# Revit family: Mixer-Basin-Dorf Epic-Wall1
name_source: partatom
category: Plumbing Fixtures
revit_build: Autodesk Revit Architecture 2012 (Build: 20110916_2132(x64)
units: mm (PartAtom-declared; Revit-internal decimal feet)

## types (2) — shared parameters
Assembly Code = D2020300
CW Connection = Yes
CWFU = 2
Connector Radius = 10 mm  [stored 0.0328084 ft]
Default Elevation = 1200 mm
Description = Fully featured cartridge, Chrome finish, Water efficient, Longer reach for sink versatility, European hoses
HW Connection = Yes
HWFU = 2
Manufacturer = Dorf
Material_ANZRS = Metal-Chrome-Caroma
URL = http://www.dorf.com.au
Vent Connection = No
WELSRating_ANZRS = WELS 5 star rated, 6L/min
Waste Connection = No
zero-valued in all types: Cost

## per-type parameters (varying)
| type | Large | Model | Spout | Type Comments |
| 180mm Outlet | No | 6410.045A | 180 mm  [stored 0.590551 ft] | Epic Wall Basin Mixer 180mm Outlet |
| 240mm Outlet | Yes | 6411.045A | 240 mm  [stored 0.787402 ft] | Epic Wall Basin Mixer 240mm Outlet |

note: [stored X ft] marks values corroborated as IEEE doubles in the binary element streams (Revit-internal decimal feet)

## geometry (parser evidence)
native form markers: Blend x4, Sweep x1
no freeform markers — native parametric forms only
